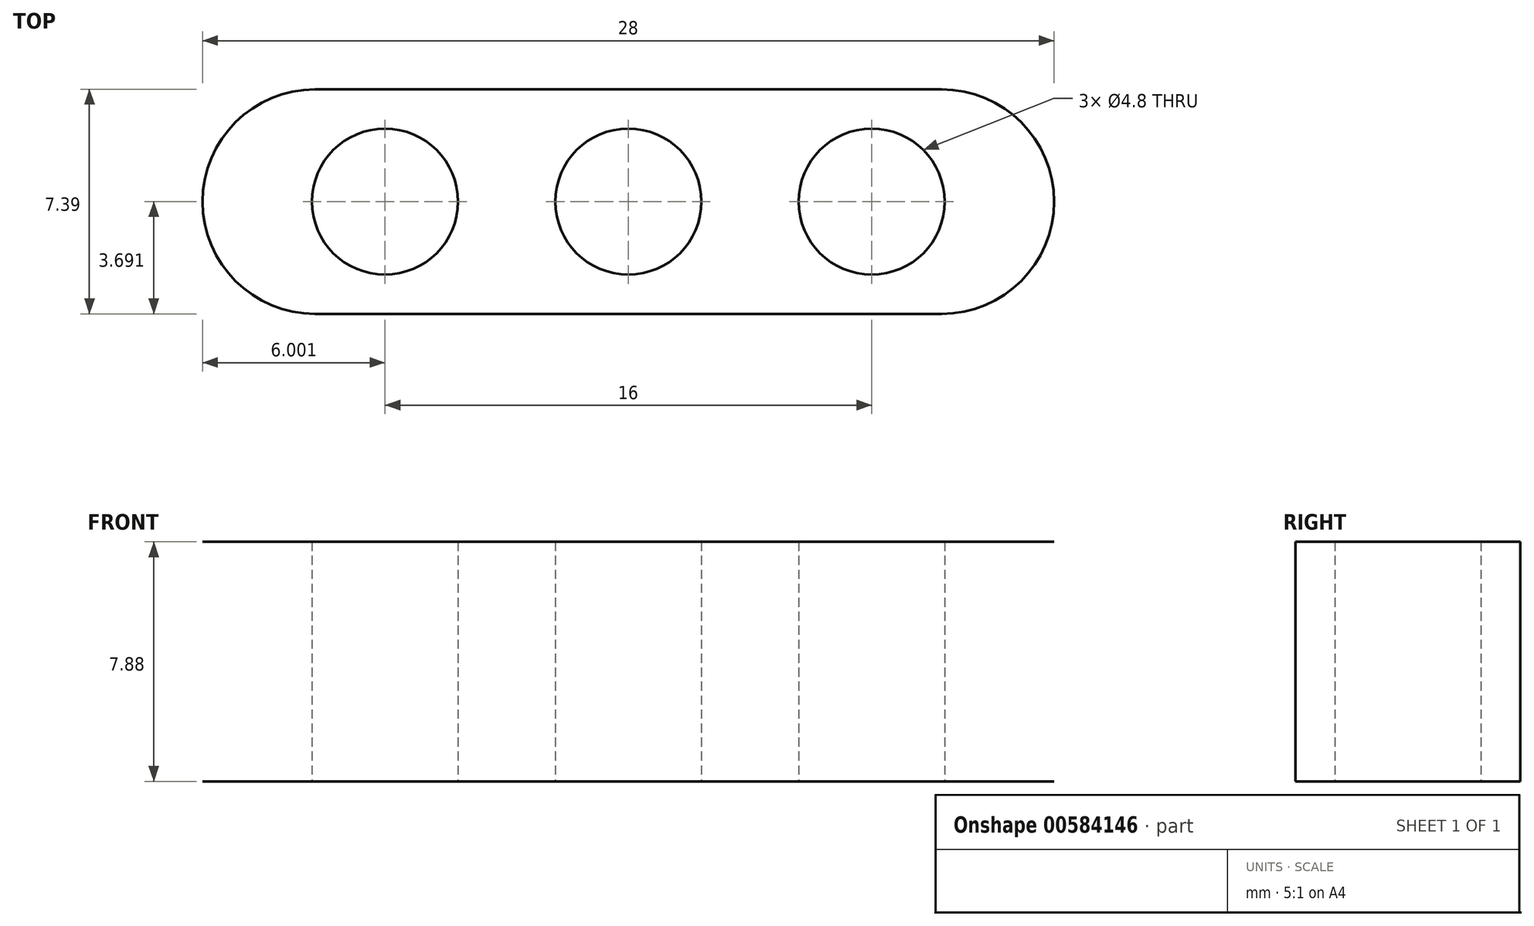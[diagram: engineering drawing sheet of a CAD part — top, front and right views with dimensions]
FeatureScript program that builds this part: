
annotation { "Feature Type Name" : "Feature", "Feature Type Description" : "" }
export const myFeature = defineFeature(function(context is Context, id is Id, definition is map)
    precondition{}
    {
        {
            var Q0;
            Q0=qCreatedBy(makeId("Top.planeOp"),FACE);
            var sketch = newSketch(context, id + "F0", { "sketchPlane" : qUnion([Q0])});
            skLineSegment(sketch, "E0", {"start": v(-28.72, 9.1) * mm, "end": v(-28.72, -19.18) * mm, "construction": true});
            skLineSegment(sketch, "E1", {"start": v(-28.72, -19.18) * mm, "end": v(-29.11, -19.18) * mm, "construction": true});
            skLineSegment(sketch, "E2", {"start": v(-1.18, -2.09) * mm, "end": v(-47.58, -2.09) * mm, "construction": true});
            skLineSegment(sketch, "E3", {"start": v(-47.58, -2.09) * mm, "end": v(-47.58, -1.54) * mm, "construction": true});
            skLineSegment(sketch, "E4", {"start": v(-28.72, 1.6) * mm, "end": v(-42.72, 1.6) * mm});
            skLineSegment(sketch, "E5", {"start": v(-42.72, 1.6) * mm, "end": v(-42.72, -2.09) * mm});
            skArc(sketch, "E6", {"start": v(-28.72, 0.31) * mm, "mid": v(-31.12, -2.09) * mm, "end": v(-28.72, -4.49) * mm});
            skCircle(sketch, "E7", {"center": v(-36.72, -2.09) * mm, "radius": 2.4 * mm});
            skLineSegment(sketch, "E8.direction1", {"start": v(-36.72, -2.09) * mm, "end": v(-44.72, -2.09) * mm, "construction": true});
            skLineSegment(sketch, "E9.MirrorCS", {"start": v(-28.72, -5.78) * mm, "end": v(-42.72, -5.78) * mm});
            skLineSegment(sketch, "E10.MirrorCS", {"start": v(-42.72, -5.78) * mm, "end": v(-42.72, -2.09) * mm});
            skLineSegment(sketch, "E11.MirrorCS", {"start": v(-9.86, -2.09) * mm, "end": v(-9.86, -1.54) * mm, "construction": true});
            skLineSegment(sketch, "E12.MirrorCS", {"start": v(-56.26, -2.09) * mm, "end": v(-9.86, -2.09) * mm, "construction": true});
            skArc(sketch, "E13.MirrorCS", {"start": v(-28.72, 0.31) * mm, "mid": v(-26.32, -2.09) * mm, "end": v(-28.72, -4.49) * mm});
            skCircle(sketch, "E14.MirrorC", {"center": v(-20.72, -2.09) * mm, "radius": 2.4 * mm});
            skLineSegment(sketch, "E15.MirrorCS", {"start": v(-28.72, 1.6) * mm, "end": v(-14.72, 1.6) * mm});
            skLineSegment(sketch, "E16.MirrorCS", {"start": v(-14.72, 1.6) * mm, "end": v(-14.72, -2.09) * mm});
            skLineSegment(sketch, "E17.MirrorCS", {"start": v(-14.72, -5.78) * mm, "end": v(-14.72, -2.09) * mm});
            skLineSegment(sketch, "E18.MirrorCS", {"start": v(-28.72, -5.78) * mm, "end": v(-14.72, -5.78) * mm});
            skLineSegment(sketch, "E19.MirrorCS", {"start": v(-20.72, -2.09) * mm, "end": v(-12.72, -2.09) * mm, "construction": true});
            skSolve(sketch);
        }
        {
            var Q0;
            Q0=makeQuery(id+"F0.imprint","IMPRINT",FACE,{"disambiguationData":[TD([[makeQuery(id+"F0.imprint","IMPRINT",EDGE,{"derivedFrom":sQuery(id+"F0.wireOp",EDGE,"E4")}),1.0]])]});
            extrude(context, id + "F1", {"entities" : qUnion([Q0]), "depth" : 7.88 * mm, "offsetDistance" : 25 * mm});
        }
        {
            var Q0;
            Q0=makeQuery(id+"F1.opExtrude","SWEPT_EDGE",EDGE,{"disambiguationData":[OSD([sQuery(id+"F0.wireOp",EDGE,"E15.MirrorCS"),sQuery(id+"F0.wireOp",EDGE,"E16.MirrorCS")])]});
            var Q1;
            Q1=makeQuery(id+"F1.opExtrude","SWEPT_EDGE",EDGE,{"disambiguationData":[OSD([sQuery(id+"F0.wireOp",EDGE,"E17.MirrorCS"),sQuery(id+"F0.wireOp",EDGE,"E18.MirrorCS")])]});
            var Q2;
            Q2=makeQuery(id+"F1.opExtrude","SWEPT_EDGE",EDGE,{"disambiguationData":[OSD([sQuery(id+"F0.wireOp",EDGE,"E4"),sQuery(id+"F0.wireOp",EDGE,"E5")])]});
            var Q3;
            Q3=makeQuery(id+"F1.opExtrude","SWEPT_EDGE",EDGE,{"disambiguationData":[OSD([sQuery(id+"F0.wireOp",EDGE,"E9.MirrorCS"),sQuery(id+"F0.wireOp",EDGE,"E10.MirrorCS")])]});
            fillet(context, id + "F2", {"entities" : qUnion([Q0, Q1, Q2, Q3]), "radius" : 3.7 * mm, "tangentPropagation" : true, "allowEdgeOverflow" : false});
        }
    });
